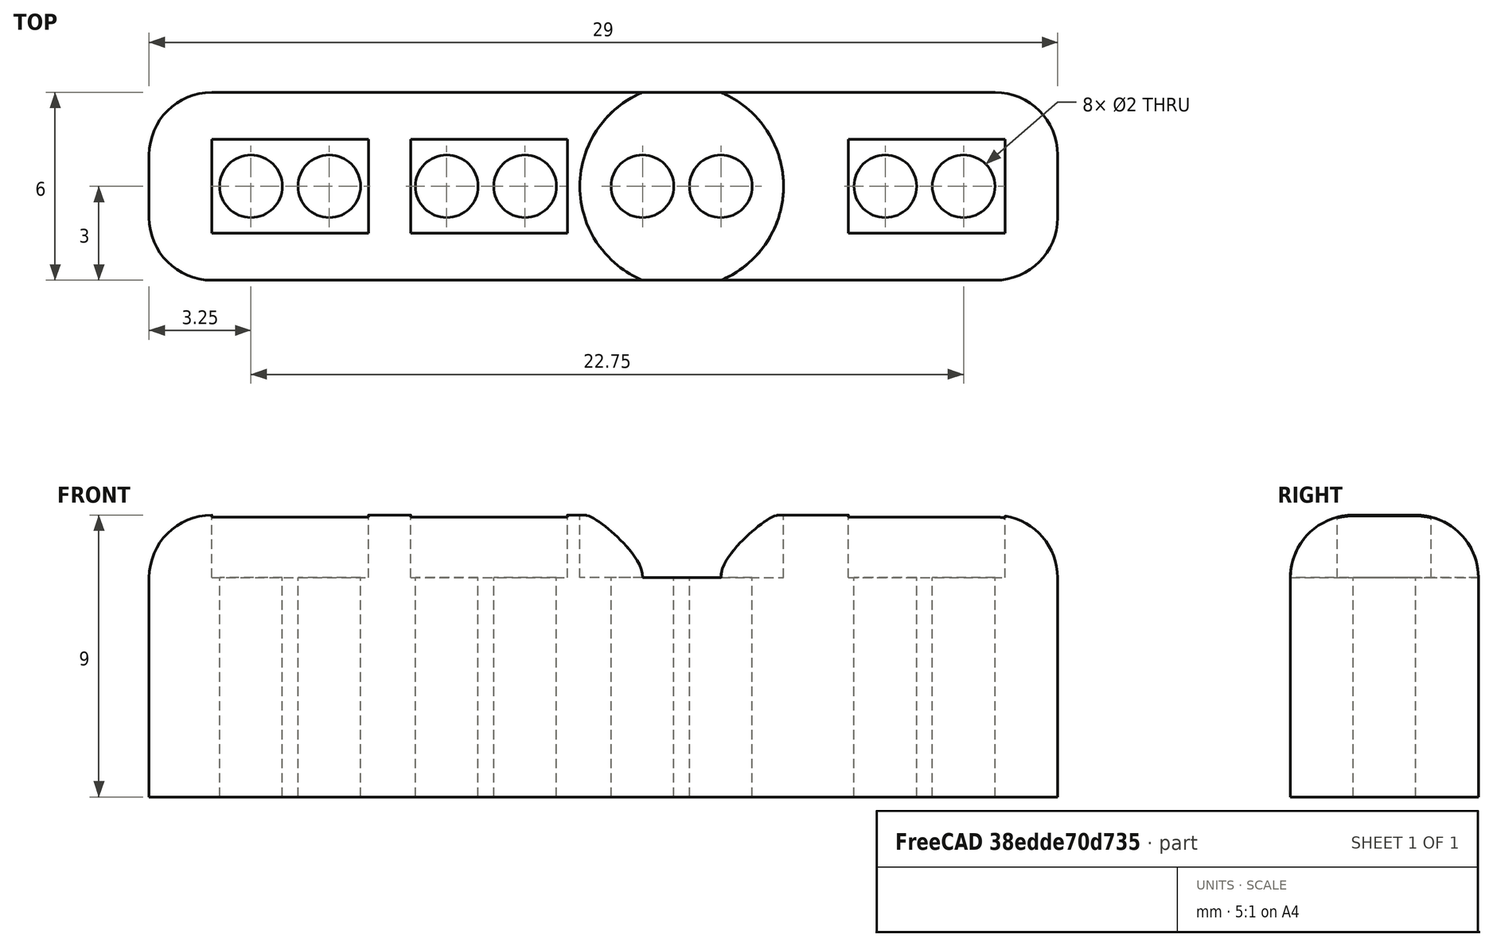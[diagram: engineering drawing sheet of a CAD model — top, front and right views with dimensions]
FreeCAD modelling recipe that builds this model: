
FCSTD DOCUMENT  (FreeCAD 0.19R24276 (Git))
Label: standoff
License: All rights reserved
LicenseURL: http://en.wikipedia.org/wiki/All_rights_reserved
objects: Part::Cylinder×9, Part::MultiFuse×5, Part::Box×4, Part::Fillet×1, Part::Cut×1
note: 20 computed .brp shape members not serialized (recipe doc carries the construction recipe); baked Part::Feature solids carry a one-line shape summary decoded from their .brp

FEATURE [Part::Box] Box  label="Cube"
  AttacherType = Attacher::AttachEngine3D
  Height = 9
  Length = 29
  Width = 6
FEATURE [Part::Box] Box001  label="Cube001"
  AttacherType = Attacher::AttachEngine3D
  Height = 10
  Length = 5
  Placement = pos=(2,1.5,7) rot=(0,0,1;0rad)
  Width = 3
FEATURE [Part::Box] Box002  label="Cube002"
  AttacherType = Attacher::AttachEngine3D
  Height = 10
  Length = 5
  Placement = pos=(8.35,1.5,7) rot=(0,0,1;0rad)
  Width = 3
FEATURE [Part::Box] Box003  label="Cube003"
  AttacherType = Attacher::AttachEngine3D
  Height = 10
  Length = 5
  Placement = pos=(22.32,1.5,7) rot=(0,0,1;0rad)
  Width = 3
FEATURE [Part::Cylinder] Cylinder
  Angle = 360
  AttacherType = Attacher::AttachEngine3D
  Height = 10
  Placement = pos=(17,3,7) rot=(0,0,1;0rad)
  Radius = 3.25
FEATURE [Part::Cylinder] Cylinder001
  Angle = 360
  AttacherType = Attacher::AttachEngine3D
  Height = 20
  Placement = pos=(3.25,3,0) rot=(0,0,1;0rad)
  Radius = 1
FEATURE [Part::Cylinder] Cylinder002
  Angle = 360
  AttacherType = Attacher::AttachEngine3D
  Height = 20
  Placement = pos=(5.75,3,0) rot=(0,0,1;0rad)
  Radius = 1
FEATURE [Part::MultiFuse] Fusion
  Shapes = -> [Cylinder001,Cylinder002]
FEATURE [Part::Cylinder] Cylinder003
  Angle = 360
  AttacherType = Attacher::AttachEngine3D
  Height = 20
  Placement = pos=(3.25,3,0) rot=(0,0,1;0rad)
  Radius = 1
FEATURE [Part::Cylinder] Cylinder004
  Angle = 360
  AttacherType = Attacher::AttachEngine3D
  Height = 20
  Placement = pos=(5.75,3,0) rot=(0,0,1;0rad)
  Radius = 1
FEATURE [Part::MultiFuse] Fusion001
  Placement = pos=(6.25,0,0) rot=(0,0,1;0rad)
  Shapes = -> [Cylinder003,Cylinder004]
FEATURE [Part::Cylinder] Cylinder005
  Angle = 360
  AttacherType = Attacher::AttachEngine3D
  Height = 20
  Placement = pos=(3.25,3,0) rot=(0,0,1;0rad)
  Radius = 1
FEATURE [Part::Cylinder] Cylinder006
  Angle = 360
  AttacherType = Attacher::AttachEngine3D
  Height = 20
  Placement = pos=(5.75,3,0) rot=(0,0,1;0rad)
  Radius = 1
FEATURE [Part::MultiFuse] Fusion002
  Placement = pos=(20.25,0,0) rot=(0,0,1;0rad)
  Shapes = -> [Cylinder005,Cylinder006]
FEATURE [Part::Cylinder] Cylinder007
  Angle = 360
  AttacherType = Attacher::AttachEngine3D
  Height = 20
  Placement = pos=(3.25,3,0) rot=(0,0,1;0rad)
  Radius = 1
FEATURE [Part::Cylinder] Cylinder008
  Angle = 360
  AttacherType = Attacher::AttachEngine3D
  Height = 20
  Placement = pos=(5.75,3,0) rot=(0,0,1;0rad)
  Radius = 1
FEATURE [Part::MultiFuse] Fusion003
  Placement = pos=(12.5,0,0) rot=(0,0,1;0rad)
  Shapes = -> [Cylinder007,Cylinder008]
FEATURE [Part::Fillet] Fillet
  Base = -> Box
  Edges = 8 edges r=2: [Edge1,Edge2,Edge3,Edge5,Edge6,Edge7,Edge10,Edge12]
FEATURE [Part::MultiFuse] Fusion004
  Shapes = -> [Fusion003,Box001,Box002,Box003,Cylinder,Fusion,Fusion001,Fusion002]
FEATURE [Part::Cut] Cut  label="standoff"
  Base = -> Fillet
  Tool = -> Fusion004
